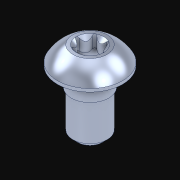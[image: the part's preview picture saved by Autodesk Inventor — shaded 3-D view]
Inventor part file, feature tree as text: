
AUTODESK INVENTOR PART (.ipt)
format: ipt  version: 2021 (Build 250183000, 183)  size: 294,912 bytes
history: native  units: in
note: dims shown in document units (in); Inventor stores cm internally (conversion verified against a paired STEP export)
features: other x19, sketch x6, extrude x1, thread x1, projected_geometry x1
ambient origin geometry x8: Origin, YZ Plane, XZ Plane, XY Plane, X Axis, Y Axis, Z Axis, Center Point
bodies: Solid1 (feature_tree), Body (feature_tree)
feature tree (28):
  other  "Table"
  other  "SScrew Shoulder Smooth .290 x .09"
  other  "SScrew Shoulder Smooth .375 x .12"
  other  "SScrew Shoulder Smooth .500 x .04"
  other  "SScrew Shoulder Smooth .500 x .18"
  other  "SScrew Shoulder Smooth 1.000 x .12"
  other  "SScrew Shoulder Smooth 1.500 x .18"
  other  "SScrew Shoulder Smooth 2.000 x .04"
  other  "SScrew Shoulder Threaded .290 x .09"
  other  "SScrew Shoulder Threaded .375 x .12"
  other  "SScrew Shoulder Threaded .500 x .04"
  other  "SScrew Shoulder Threaded .500 x .18"
  other  "SScrew Shoulder Threaded 1.000 x .12"
  other  "SScrew Shoulder Threaded 1.500 x .18"
  other  "SScrew Shoulder Threaded 2.000 x .04"
  other  "Head"
  extrude  "Hex"  Depth=0.164in
  other  "Head Chamfer"
  thread  "Thread"  [1 undecoded]
  other  "Tapered End"
  other  "Shoulder"
  sketch  "Sketch1"  dims[d1=0.0in d4=0.164in d5=0.156in]
  sketch  "Sketch2"  dims[d6=0.015in]
  sketch  "Sketch4"  dims[d13=0.004in]
  sketch  "Sketch5"  dims[d14=0.082in]
  sketch  "Sketch6"  dims[d15=0.087in]
  projected_geometry  "Projected Loop1"
  sketch  "Sketch8"  dims[d16=0.0in d17=0.066in d20=90.0deg d22=0.07in d23=0.0in d29=0.066in d30=90.0deg d31=30.0deg d32=60.0deg d37=0.031in d38=0.315in d39=11.811in d40=0.0in d41=90.0deg d42=90.0deg d43=0.0in d44=0.0in d46=0.0312in d49=0.0585in d50=135.0deg d53=90.0deg d54=0.0027in d55=0.0205in d56=0.0039in d57=0.1378in d58=0.115in d59=0.163in d60=1.1811in d62=120.0deg d69=0.09in d70=0.09in d71=90.0deg]
note: 1 required parameter value undecoded (feature->parameter linkage not recoverable at this tier; creation-order binding heuristic only, values carry confidence <= 0.55)
